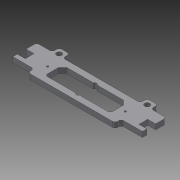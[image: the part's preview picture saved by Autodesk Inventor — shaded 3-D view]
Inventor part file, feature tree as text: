
AUTODESK INVENTOR PART (.ipt)
format: ipt  version: 2016 (Build 200138000, 138)  size: 198,144 bytes
history: native  units: mm
features: extrude x8, sketch x8, chamfer x2, mirror x1, fillet x1
ambient origin geometry x8: Origin, YZ Plane, XZ Plane, XY Plane, X Axis, Y Axis, Z Axis, Center Point
bodies: Solid1 (feature_tree)
feature tree (20):
  extrude  "Extrusion1"  Depth=34.0mm
  extrude  "Extrusion2"  Depth=74.0mm
  extrude  "Extrusion3"  Depth=6.0mm TaperAngle=0.0deg
  extrude  "Extrusion4"  Depth=9.0mm
  extrude  "Extrusion5"  Depth=9.0mm
  extrude  "Extrusion6"  Depth=6.0mm
  extrude  "Extrusion7"  Depth=12.0mm
  mirror  "Mirror1"
  chamfer  "Chamfer3"  Distance=2.0mm
  chamfer  "Chamfer4"  Distance=6.0mm
  fillet  "Fillet2"  Radius=9.0mm
  extrude  "Extrusion8"  Depth=10.0mm
  sketch  "Sketch1"  dims[d0=147.0mm d1=34.0mm]
  sketch  "Sketch2"  dims[d2=6.0mm d3=0.0mm d4=74.0mm]
  sketch  "Sketch3"  dims[d5=20.0mm d6=6.0mm d7=0.0mm]
  sketch  "Sketch4"  dims[d8=5.0mm d10=9.0mm]
  sketch  "Sketch5"  dims[d11=5.0mm d12=9.0mm]
  sketch  "Sketch6"  dims[d13=6.0mm d14=0.0mm d15=6.0mm]
  sketch  "Sketch7"  dims[d16=12.0mm d17=12.0mm]
  sketch  "Sketch8"  dims[d18=50.0mm d19=2.0mm d20=6.0mm d21=0.0mm d22=9.0mm d23=10.0mm d24=6.0mm d25=0.0mm d26=24.0mm d28=7.0mm d29=6.0mm d30=0.0mm d31=2.25mm d32=44.1mm d33=6.0mm d34=0.0mm d42=5.0mm d43=2.0mm d44=45.0deg d45=2.0mm d46=2.0mm d47=45.0deg d48=3.0mm d49=10.0mm d50=0.0mm]
